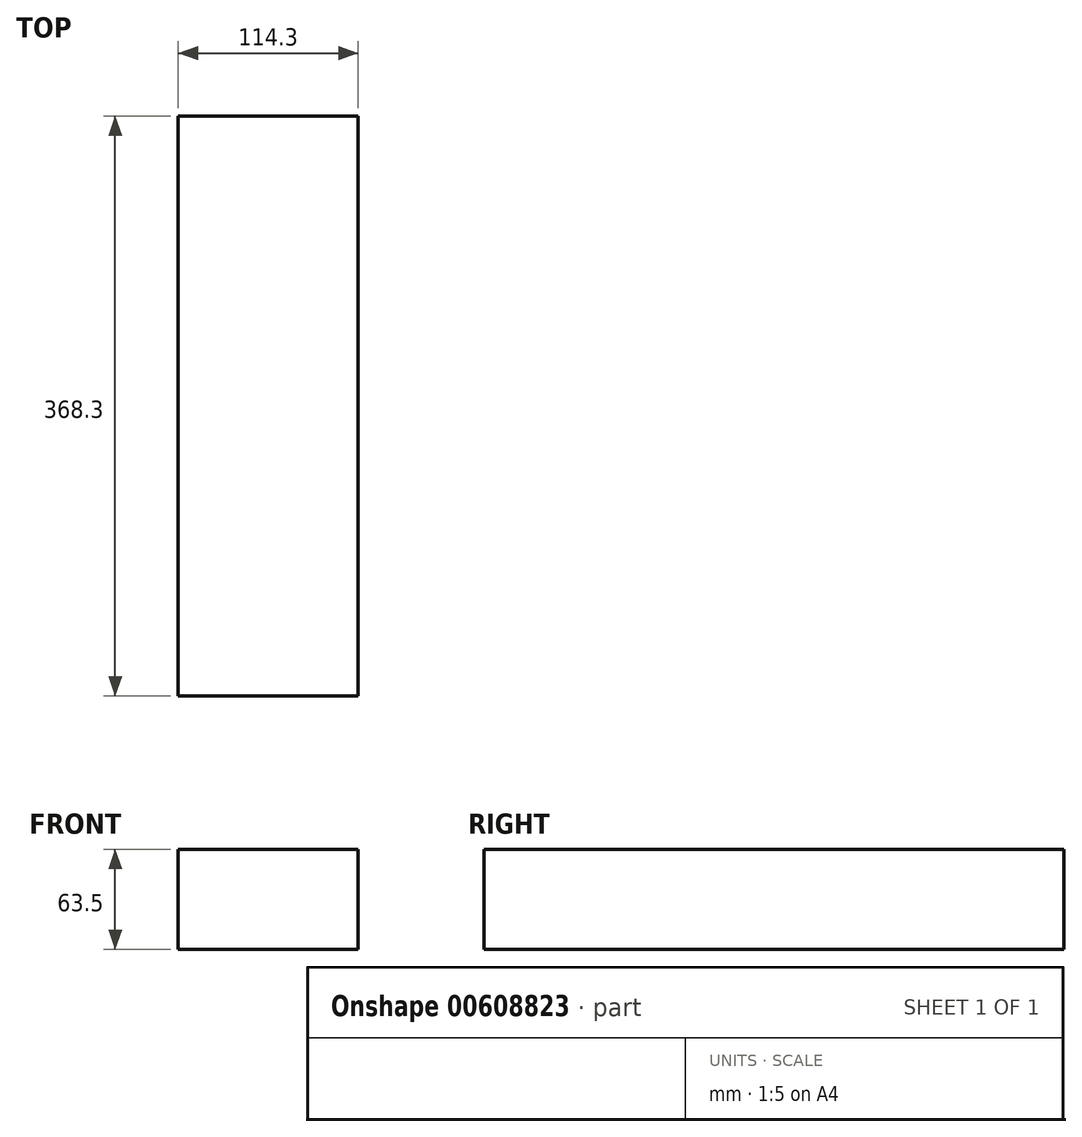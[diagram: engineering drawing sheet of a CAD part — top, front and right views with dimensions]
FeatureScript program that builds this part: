
annotation { "Feature Type Name" : "Feature", "Feature Type Description" : "" }
export const myFeature = defineFeature(function(context is Context, id is Id, definition is map)
    precondition{}
    {
        {
            var Q0;
            Q0=qCreatedBy(makeId("Top.planeOp"),FACE);
            var sketch = newSketch(context, id + "F0", { "sketchPlane" : qUnion([Q0])});
            skLineSegment(sketch, "E0.bottom", {"start": v(57.15, -184.15) * mm, "end": v(-57.15, -184.15) * mm});
            skLineSegment(sketch, "E0.top", {"start": v(57.15, 184.15) * mm, "end": v(-57.15, 184.15) * mm});
            skLineSegment(sketch, "E0.left", {"start": v(57.15, -184.15) * mm, "end": v(57.15, 184.15) * mm});
            skLineSegment(sketch, "E0.right", {"start": v(-57.15, -184.15) * mm, "end": v(-57.15, 184.15) * mm});
            skPoint(sketch, "E0.middle", {"position": v(0, 0) * mm});
            skSolve(sketch);
        }
        {
            var Q0;
            Q0 = qSketchRegion(id + "F0", true);
            extrude(context, id + "F1", {"entities" : qUnion([Q0]), "depth" : 63.5 * mm, "offsetDistance" : 25.4 * mm});
        }
    });
